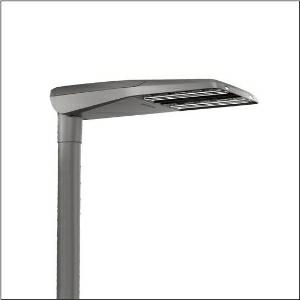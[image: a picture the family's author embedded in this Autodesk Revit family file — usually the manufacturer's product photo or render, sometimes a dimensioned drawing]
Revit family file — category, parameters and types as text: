
# Revit family: streetlight_sl_11_iq_midi___st1_2a_5xc3a21f08me_5047
name_source: partatom
category: Lighting Fixtures
units: mm (PartAtom-declared; Revit-internal decimal feet)

## family parameters
Cut with Voids When Loaded = No
Host = Face
Light Source = No
Part Type = Normal
Room Calculation Point = No
Round Connector Dimension = Use Diameter
Shared = No

## types (1)
- --- (1 x LED, 14840 lm, 124.7 W, 2200K)
    Apparent Load = 125 VA
    CIE Flux Codes = 32 70 96 100 100
    Color Rendering = 70
    Color Temperature = 2200K
    Default Elevation = 1800 mm
    Description = Streetlight SL 11 iQ midi, mast luminaire, primary light control with 3 zone facetted reflector, of plastic, silver coated, highly specular, primary optical cover: cover, of PMMA, transparent, light distribution: ST1.2a, light emission: direct distribution, primary light characteristic: asymmetric, installation type: post-top, side-entry, lamps: LED, High Power LED, rated values: 14.840lm | 124,7W | 119lm/W (begin service life); end service life: 14.840lm | 132,2W; at 50% lumin. flux: 7.420lm | 57,1W | 129,9lm/W, colour temperature: 2200K, colour rendering: CRI > 70, light colour: 722, light setting 1 begin service life: 100% | 14.840lm | 124,7W | 119lm/W | 2.200K, light setting 1 end service life: 132,2W, further light settings possible, control: Street-Remote, optimised constant luminous flux control (CLO 2.0), Desk-Remote (wireless, voltage-free reading and setting of iQ features in the workshop via application-optimized NFC function/RFID function), Light-Fading, Smart-Wire, Night-Set, Lumen-Switch, Temp-Guard, Auto-Match, with cable H07RN-F 5x 1.5mm², mains connection: 230..240V, AC, 50/60Hz, connection cable pre-assembled, cable length: 12,5m, luminaire housing, of diecast aluminium, powder-coated, Siteco® metallic grey (DB 702S), please order mast flange separately, inclination adjustable without tools: 0°, 5°, 10°, 15° (post-top) | 0°, -5°, -10°, -15° (side-entry), sealing non-destructively replaceable, multi-level sealing system, length: 780mm, width: 376mm, height: 118mm, mast flange for spigot size: 42mm (side-entry): 5XC10008XM4, 60/48mm (side-entry/post-top): 5XC10108XM2, 76/60mm (side-entry/post-top): 5XC10108XM1, equipment: Power, protection rating (complete): IP66, insulation class (complete): insulation class II (safety insulation), certification: CE, ENEC, ENEC+, VDE, impact resistance: IK10, permissible operating ambient temperature for outdoor applications: -25..+50°C, standard-compliant lighting for roads and squares, Environmental Product Declaration (EPD) tested and certified by an independent institute, packaging unit: 1 piece

Light Distribution: ST1.2a
    Height = 118 mm
    Lamp = 1 x LED
    Lamp Light Flux = 14840 lm
    Lamp Power = 124.7 W
    Lamp count = 1
    Length = 780 mm
    Luminous efficacy = 119 lm/W
    Manufacturer = Siteco
    ModVariant = No
    Model = 5XC3A21F08ME
    Number of Poles = 1
    OnlyDefault = Yes
    Power Factor = 1
    Product Name = Streetlight SL 11 iQ midi | ST1.2a
    Product group = mast luminaire | pylon top
    ProductGroupID = 6100
    Protection Class = Protection class II
    Protection Degree = IP 66
    RLX_Detail_Level = 1
    RLX_Emergency_Light_Flux = 0 lm
    RLX_Emergency_Type = 0
    RLX_Emergency_Type_DB = No
    RlxData = <blob elided: 70841 chars, md5=37ef8a00>
    Socket = socket
    Standby Power = 0 W
    System Light Flux = 14841 lm
    System Power = 125 W
    Type Comments = factory setting: luminous flux: 100 % | dim-lin: 254 | 557 mA
    Type Image = l_1005960.jpg
    URL = http://relux.com
    VarID = @adj_129428
    Voltage = 0 V
    Weight = 0.00 kg
    Width = 376 mm

## geometry (parser evidence)
native form markers: Blend x4, Sweep x11
no freeform markers — native parametric forms only
